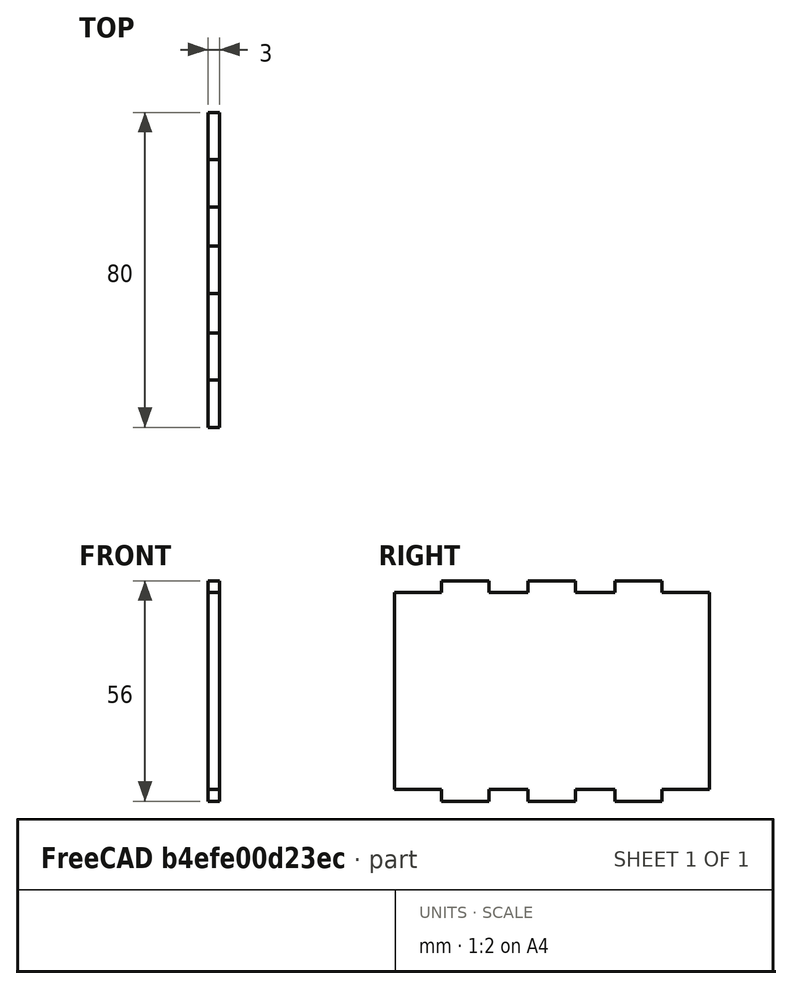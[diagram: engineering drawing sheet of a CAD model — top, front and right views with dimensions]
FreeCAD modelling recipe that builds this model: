
FCSTD DOCUMENT  (FreeCAD 0.19R)
Label: box_right
License: Creative Commons Attribution-ShareAlike
LicenseURL: http://creativecommons.org/licenses/by-sa/4.0/
objects: PartDesign::SubShapeBinder×2, PartDesign::Pad×2, PartDesign::Mirrored×1, PartDesign::LinearPattern×1, PartDesign::MultiTransform×1, PartDesign::Body×1, App::Part×1
note: 10 computed .brp shape members not serialized (recipe doc carries the construction recipe); baked Part::Feature solids carry a one-line shape summary decoded from their .brp
EXTERNAL_REF file=base.FCStd obj=Part
EXTERNAL_REF file=base.FCStd obj=Spreadsheet
EXTERNAL_REF file=base.FCStd obj=Sketch004

FEATURE [PartDesign::SubShapeBinder] Binder  label="right_outline_Binder"
  BindMode = 0
  ClaimChildren = false
  Context = -> Part [Body.Binder.]
  Fuse = false
  MakeFace = true
  PartialLoad = false
  Relative = true
  Support = -> [<external base.FCStd>#Part[Body.Sketch002.]]
  _Version = 2
FEATURE [PartDesign::Pad] Pad
  Direction = (1,1,1)
  Length = 3
  Length2 = 100
  Profile = -> Binder
  Type = 0
  expr: Length = <<base>>#<<base_values>>.wood
FEATURE [PartDesign::SubShapeBinder] Binder001  label="joint_right_top_Binder001"
  BindMode = 0
  ClaimChildren = false
  Context = -> Part [Body.Binder001.]
  Fuse = false
  MakeFace = true
  PartialLoad = false
  Relative = true
  Support = -> [<external base.FCStd>#Part[Body.Sketch005.]]
  _Version = 2
FEATURE [PartDesign::Pad] Pad001
  BaseFeature = -> Pad
  Direction = (1,1,1)
  Length = 3
  Length2 = 100
  Profile = -> Binder001
  Type = 0
  expr: Length = base#<<base_values>>.wood
FEATURE [PartDesign::Mirrored] Mirrored
  MirrorPlane = -> XY_Plane001
FEATURE [PartDesign::LinearPattern] LinearPattern
  Direction = -> Y_Axis001
  Length = 44
  Occurrences = 3
  expr: Length = base#<<joint_right_base>>.Constraints.array_y
FEATURE [PartDesign::MultiTransform] MultiTransform
  BaseFeature = -> Pad001
  Originals = -> [Pad001]
  Refine = true
  Transformations = -> [Mirrored,LinearPattern]
FEATURE [PartDesign::Body] Body  label="box_right_Body"
  Group = -> [Binder,Pad,Binder001,Pad001,MultiTransform,Mirrored,LinearPattern]
  Origin = -> Origin001
  Tip = -> MultiTransform
FEATURE [App::Part] Part  label="box_right"
  Group = -> [Body]
  Origin = -> Origin
